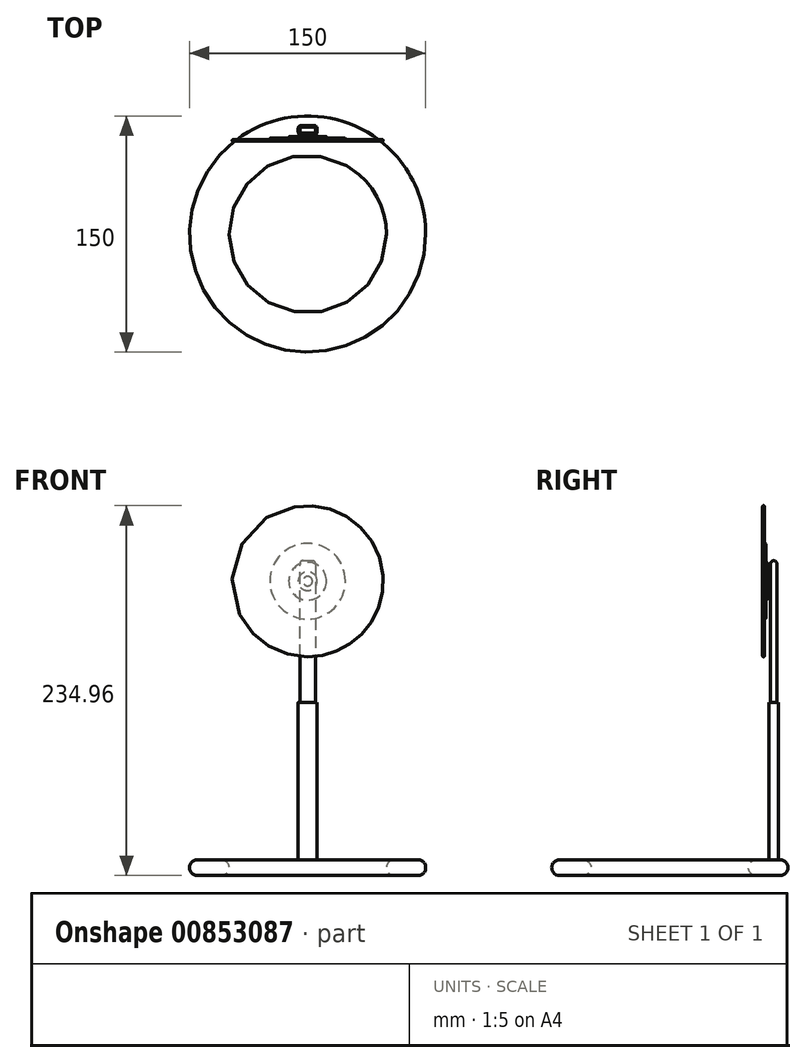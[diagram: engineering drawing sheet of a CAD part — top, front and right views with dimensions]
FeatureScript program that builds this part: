
annotation { "Feature Type Name" : "Feature", "Feature Type Description" : "" }
export const myFeature = defineFeature(function(context is Context, id is Id, definition is map)
    precondition{}
    {
        {
            var Q0;
            Q0=qCreatedBy(makeId("Top.planeOp"),FACE);
            var sketch = newSketch(context, id + "F0", { "sketchPlane" : qUnion([Q0])});
            skLineSegment(sketch, "E0", {"start": v(-75, 0) * mm, "end": v(75, 0) * mm, "construction": true});
            skCircle(sketch, "E1", {"center": v(0, 0) * mm, "radius": 75 * mm});
            skCircle(sketch, "E2", {"center": v(0, 0) * mm, "radius": 50 * mm});
            skLineSegment(sketch, "E3", {"start": v(0, 0) * mm, "end": v(0, 140.63) * mm, "construction": true});
            skSolve(sketch);
        }
        {
            var Q0;
            Q0 = qSketchRegion(id + "F0", true);
            extrude(context, id + "F1", {"entities" : qUnion([Q0]), "depth" : 10 * mm, "offsetDistance" : 25 * mm});
        }
        {
            var Q0;
            Q0=makeQuery(id+"F1.opExtrude","CAP_EDGE",EDGE,{"disambiguationData":[OSD([sQuery(id+"F0.wireOp",EDGE,"E1")])],"isStart":false});
            var Q1;
            Q1=makeQuery(id+"F1.opExtrude","CAP_EDGE",EDGE,{"disambiguationData":[OSD([sQuery(id+"F0.wireOp",EDGE,"E2")])],"isStart":false});
            var Q2;
            Q2=makeQuery(id+"F1.opExtrude","CAP_EDGE",EDGE,{"disambiguationData":[OSD([sQuery(id+"F0.wireOp",EDGE,"E1")])],"isStart":true});
            var Q3;
            Q3=makeQuery(id+"F1.opExtrude","CAP_EDGE",EDGE,{"disambiguationData":[OSD([sQuery(id+"F0.wireOp",EDGE,"E2")])],"isStart":true});
            fillet(context, id + "F2", {"entities" : qUnion([Q0, Q1, Q2, Q3]), "radius" : 5 * mm, "tangentPropagation" : true, "allowEdgeOverflow" : false});
        }
        {
            var Q0;
            Q0=makeQuery(id+"F1.opExtrude","CAP_FACE",FACE,{"disambiguationData":[OSD([sQuery(id+"F0.wireOp",EDGE,"E1"),sQuery(id+"F0.wireOp",EDGE,"E2")])],"isStart":false});
            var sketch = newSketch(context, id + "F3", { "sketchPlane" : qUnion([Q0])});
            skLineSegment(sketch, "E4", {"start": v(0, 55) * mm, "end": v(0, 63) * mm, "construction": true});
            skLineSegment(sketch, "E5", {"start": v(0, 70) * mm, "end": v(0, 69) * mm, "construction": true});
            skLineSegment(sketch, "E6", {"start": v(-6, 63) * mm, "end": v(6, 63) * mm});
            skLineSegment(sketch, "E7", {"start": v(-6, 69) * mm, "end": v(6, 69) * mm});
            skLineSegment(sketch, "E8", {"start": v(-6, 69) * mm, "end": v(-6, 63) * mm});
            skLineSegment(sketch, "E9", {"start": v(6, 69) * mm, "end": v(6, 63) * mm});
            skSolve(sketch);
        }
        {
            var Q0;
            Q0=makeQuery(id+"F3.imprint","IMPRINT",FACE,{"disambiguationData":[TD([[makeQuery(id+"F3.imprint","IMPRINT",EDGE,{"derivedFrom":sQuery(id+"F3.wireOp",EDGE,"E6")}),1.0]])]});
            extrude(context, id + "F4", {"entities" : qUnion([Q0]), "operationType" : NewBodyOperationType.ADD, "depth" : 100 * mm, "offsetDistance" : 25 * mm});
        }
        {
            var Q0;
            Q0=makeQuery(id+"F4.opExtrude","SWEPT_EDGE",EDGE,{"disambiguationData":[OSD([sQuery(id+"F3.wireOp",EDGE,"E7"),sQuery(id+"F3.wireOp",EDGE,"E9")])]});
            var Q1;
            Q1=makeQuery(id+"F4.opExtrude","SWEPT_EDGE",EDGE,{"disambiguationData":[OSD([sQuery(id+"F3.wireOp",EDGE,"E6"),sQuery(id+"F3.wireOp",EDGE,"E9")])]});
            var Q2;
            Q2=makeQuery(id+"F4.opExtrude","SWEPT_EDGE",EDGE,{"disambiguationData":[OSD([sQuery(id+"F3.wireOp",EDGE,"E7"),sQuery(id+"F3.wireOp",EDGE,"E8")])]});
            var Q3;
            Q3=makeQuery(id+"F4.opExtrude","SWEPT_EDGE",EDGE,{"disambiguationData":[OSD([sQuery(id+"F3.wireOp",EDGE,"E6"),sQuery(id+"F3.wireOp",EDGE,"E8")])]});
            fillet(context, id + "F5", {"entities" : qUnion([Q0, Q1, Q2, Q3]), "radius" : 2 * mm, "tangentPropagation" : true, "allowEdgeOverflow" : false});
        }
        {
            var Q0;
            Q0=makeQuery(id+"F4.opExtrude","CAP_FACE",FACE,{"disambiguationData":[OSD([sQuery(id+"F3.wireOp",EDGE,"E6"),sQuery(id+"F3.wireOp",EDGE,"E7"),sQuery(id+"F3.wireOp",EDGE,"E8"),sQuery(id+"F3.wireOp",EDGE,"E9")])],"isStart":false});
            var sketch = newSketch(context, id + "F6", { "sketchPlane" : qUnion([Q0])});
            skLineSegment(sketch, "E10", {"start": v(5, 68) * mm, "end": v(-5, 68) * mm});
            skLineSegment(sketch, "E11", {"start": v(-5, 64) * mm, "end": v(-5, 68) * mm});
            skLineSegment(sketch, "E12", {"start": v(-5, 64) * mm, "end": v(5, 64) * mm});
            skLineSegment(sketch, "E13", {"start": v(5, 64) * mm, "end": v(5, 68) * mm});
            skSolve(sketch);
        }
        {
            var Q0;
            Q0=makeQuery(id+"F6.imprint","IMPRINT",FACE,{"disambiguationData":[TD([[makeQuery(id+"F6.imprint","IMPRINT",EDGE,{"derivedFrom":sQuery(id+"F6.wireOp",EDGE,"E10")}),1.0]])]});
            extrude(context, id + "F7", {"entities" : qUnion([Q0]), "operationType" : NewBodyOperationType.ADD, "depth" : 90 * mm, "offsetDistance" : 25 * mm});
        }
        {
            var Q0;
            Q0=makeQuery(id+"F7.opExtrude","SWEPT_EDGE",EDGE,{"disambiguationData":[OSD([sQuery(id+"F6.wireOp",EDGE,"E12"),sQuery(id+"F6.wireOp",EDGE,"E13")])]});
            var Q1;
            Q1=makeQuery(id+"F7.opExtrude","SWEPT_EDGE",EDGE,{"disambiguationData":[OSD([sQuery(id+"F6.wireOp",EDGE,"E10"),sQuery(id+"F6.wireOp",EDGE,"E13")])]});
            var Q2;
            Q2=makeQuery(id+"F7.opExtrude","SWEPT_EDGE",EDGE,{"disambiguationData":[OSD([sQuery(id+"F6.wireOp",EDGE,"E10"),sQuery(id+"F6.wireOp",EDGE,"E11")])]});
            var Q3;
            Q3=makeQuery(id+"F7.opExtrude","SWEPT_EDGE",EDGE,{"disambiguationData":[OSD([sQuery(id+"F6.wireOp",EDGE,"E11"),sQuery(id+"F6.wireOp",EDGE,"E12")])]});
            var Q4;
            Q4=makeQuery(id+"F7.opExtrude","CAP_EDGE",EDGE,{"disambiguationData":[OSD([sQuery(id+"F6.wireOp",EDGE,"E11")])],"isStart":false});
            var Q5;
            Q5=makeQuery(id+"F7.opExtrude","CAP_EDGE",EDGE,{"disambiguationData":[OSD([sQuery(id+"F6.wireOp",EDGE,"E13")])],"isStart":false});
            var Q6;
            Q6=makeQuery(id+"F7.opExtrude","CAP_EDGE",EDGE,{"disambiguationData":[OSD([sQuery(id+"F6.wireOp",EDGE,"E10")])],"isStart":false});
            var Q7;
            Q7=makeQuery(id+"F7.opExtrude","CAP_EDGE",EDGE,{"disambiguationData":[OSD([sQuery(id+"F6.wireOp",EDGE,"E12")])],"isStart":false});
            fillet(context, id + "F8", {"entities" : qUnion([Q0, Q1, Q2, Q3, Q4, Q5, Q6, Q7]), "radius" : 2 * mm, "tangentPropagation" : true, "allowEdgeOverflow" : false});
        }
        {
            var Q0;
            Q0=makeQuery(id+"F7.opExtrude","SWEPT_FACE",FACE,{"disambiguationData":[OSD([sQuery(id+"F6.wireOp",EDGE,"E12")])]});
            var sketch = newSketch(context, id + "F9", { "sketchPlane" : qUnion([Q0])});
            skLineSegment(sketch, "E14", {"start": v(0, 0) * mm, "end": v(0, 246.7) * mm, "construction": true});
            skLineSegment(sketch, "E15", {"start": v(0, 186.96) * mm, "end": v(-36.11, 186.96) * mm, "construction": true});
            skLineSegment(sketch, "E16.MirrorCS", {"start": v(0, 186.96) * mm, "end": v(36.11, 186.96) * mm, "construction": true});
            skLineSegment(sketch, "E17", {"start": v(-3, 190.97) * mm, "end": v(3, 190.97) * mm, "construction": true});
            skCircle(sketch, "E18", {"center": v(0, 186.96) * mm, "radius": 3 * mm});
            skSolve(sketch);
        }
        {
            var Q0;
            {var subQ0=sQuery(id+"F9.wireOp",EDGE,"E18");var subQ1=sQuery(id+"F6.wireOp",EDGE,"E12");var subQ2=makeQuery(id+"F7.opExtrude","SWEPT_FACE",FACE,{"disambiguationData":[OSD([subQ1])]});var subQ3=makeQuery(id+"F9.imprint","INTERSECT",VERTEX,{"derivedFrom":[makeQuery(id+"F8.opFillet","BLEND_EDGE",EDGE,{"blendedFrom":[makeQuery(id+"F7.opExtrude","SWEPT_EDGE",EDGE,{"disambiguationData":[OSD([sQuery(id+"F6.wireOp",EDGE,"E11"),subQ1])]}),subQ2],"blendedInto":[subQ2]}),subQ0]});Q0=makeQuery(id+"F9.imprint","IMPRINT",FACE,{"disambiguationData":[TD([[makeQuery(id+"F9.imprint","IMPRINT",EDGE,{"disambiguationData":[TD([[subQ3,1.0]])],"derivedFrom":subQ0}),1.0]])]});}
            extrude(context, id + "F10", {"entities" : qUnion([Q0]), "depth" : 1 * mm, "offsetDistance" : 25 * mm});
        }
        {
            var Q0;
            Q0=makeQuery(id+"F10.opExtrude","CAP_FACE",FACE,{"disambiguationData":[OSD([sQuery(id+"F9.wireOp",EDGE,"E18")])],"isStart":false});
            var sketch = newSketch(context, id + "F11", { "sketchPlane" : qUnion([Q0])});
            skCircle(sketch, "E19", {"center": v(0, 186.96) * mm, "radius": 6 * mm});
            skSolve(sketch);
        }
        {
            var Q0;
            Q0 = qSketchRegion(id + "F11", true);
            extrude(context, id + "F12", {"entities" : qUnion([Q0]), "operationType" : NewBodyOperationType.ADD, "depth" : 1 * mm, "offsetDistance" : 25 * mm});
        }
        {
            var Q0;
            Q0=makeQuery(id+"F12.opExtrude","CAP_FACE",FACE,{"disambiguationData":[OSD([sQuery(id+"F11.wireOp",EDGE,"E19")])],"isStart":false});
            var sketch = newSketch(context, id + "F13", { "sketchPlane" : qUnion([Q0])});
            skCircle(sketch, "E20", {"center": v(0, 186.96) * mm, "radius": 12 * mm});
            skSolve(sketch);
        }
        {
            var Q0;
            Q0 = qSketchRegion(id + "F13", true);
            extrude(context, id + "F14", {"entities" : qUnion([Q0]), "operationType" : NewBodyOperationType.ADD, "depth" : 1 * mm, "offsetDistance" : 25 * mm});
        }
        {
            var Q0;
            Q0=makeQuery(id+"F14.opExtrude","CAP_FACE",FACE,{"disambiguationData":[OSD([sQuery(id+"F13.wireOp",EDGE,"E20")])],"isStart":false});
            var sketch = newSketch(context, id + "F15", { "sketchPlane" : qUnion([Q0])});
            skCircle(sketch, "E21", {"center": v(0, 186.96) * mm, "radius": 24 * mm});
            skSolve(sketch);
        }
        {
            var Q0;
            Q0 = qSketchRegion(id + "F15", true);
            extrude(context, id + "F16", {"entities" : qUnion([Q0]), "operationType" : NewBodyOperationType.ADD, "depth" : 1 * mm, "offsetDistance" : 25 * mm});
        }
        {
            var Q0;
            Q0=makeQuery(id+"F16.opExtrude","CAP_FACE",FACE,{"disambiguationData":[OSD([sQuery(id+"F15.wireOp",EDGE,"E21")])],"isStart":false});
            var sketch = newSketch(context, id + "F17", { "sketchPlane" : qUnion([Q0])});
            skCircle(sketch, "E22", {"center": v(0, 186.96) * mm, "radius": 48 * mm});
            skSolve(sketch);
        }
        {
            var Q0;
            Q0 = qSketchRegion(id + "F17", true);
            extrude(context, id + "F18", {"entities" : qUnion([Q0]), "operationType" : NewBodyOperationType.ADD, "depth" : 1 * mm, "offsetDistance" : 25 * mm});
        }
        {
            var Q0;
            Q0=makeQuery(id+"F18.opExtrude","CAP_EDGE",EDGE,{"disambiguationData":[OSD([sQuery(id+"F17.wireOp",EDGE,"E22")])],"isStart":false});
            var Q1;
            Q1=makeQuery(id+"F18.opExtrude","CAP_EDGE",EDGE,{"disambiguationData":[OSD([sQuery(id+"F17.wireOp",EDGE,"E22")])],"isStart":true});
            var Q2;
            Q2=makeQuery(id+"F16.opExtrude","CAP_EDGE",EDGE,{"disambiguationData":[OSD([sQuery(id+"F15.wireOp",EDGE,"E21")])],"isStart":false});
            var Q3;
            Q3=makeQuery(id+"F16.opExtrude","CAP_EDGE",EDGE,{"disambiguationData":[OSD([sQuery(id+"F15.wireOp",EDGE,"E21")])],"isStart":true});
            var Q4;
            Q4=makeQuery(id+"F14.opExtrude","CAP_EDGE",EDGE,{"disambiguationData":[OSD([sQuery(id+"F13.wireOp",EDGE,"E20")])],"isStart":false});
            var Q5;
            Q5=makeQuery(id+"F14.opExtrude","CAP_EDGE",EDGE,{"disambiguationData":[OSD([sQuery(id+"F13.wireOp",EDGE,"E20")])],"isStart":true});
            var Q6;
            Q6=makeQuery(id+"F12.opExtrude","CAP_EDGE",EDGE,{"disambiguationData":[OSD([sQuery(id+"F11.wireOp",EDGE,"E19")])],"isStart":false});
            var Q7;
            Q7=makeQuery(id+"F12.opExtrude","CAP_EDGE",EDGE,{"disambiguationData":[OSD([sQuery(id+"F11.wireOp",EDGE,"E19")])],"isStart":true});
            var Q8;
            Q8=makeQuery(id+"F10.opExtrude","CAP_EDGE",EDGE,{"disambiguationData":[OSD([sQuery(id+"F9.wireOp",EDGE,"E18")])],"isStart":false});
            var Q9;
            Q9=makeQuery(id+"F10.opExtrude","CAP_EDGE",EDGE,{"disambiguationData":[OSD([sQuery(id+"F9.wireOp",EDGE,"E18")])],"isStart":true});
            fillet(context, id + "F19", {"entities" : qUnion([Q0, Q1, Q2, Q3, Q4, Q5, Q6, Q7, Q8, Q9]), "radius" : 0.5 * mm, "tangentPropagation" : true, "allowEdgeOverflow" : false});
        }
    });
